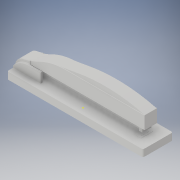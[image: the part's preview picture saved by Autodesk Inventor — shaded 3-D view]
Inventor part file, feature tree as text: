
AUTODESK INVENTOR PART (.ipt)
format: ipt  version: 2017 (Build 210142000, 142)  size: 326,656 bytes
history: native  units: in
note: dims shown in document units (in); Inventor stores cm internally (conversion verified against a paired STEP export)
features: sketch x18, extrude x16, fillet x10, plane x1, other x1
ambient origin geometry x8: Origin, YZ Plane, XZ Plane, XY Plane, X Axis, Y Axis, Z Axis, Center Point
bodies: Solid1 (feature_tree)
feature tree (46):
  extrude  "Extrusion1"  Depth=0.0394in
  fillet  "Fillet1"  Radius=0.0394in
  sketch  "Sketch3"  dims[d2=0.0394in d3=0.0394in d4=0.0394in]
  extrude  "Extrusion2"  Depth=1.5307in
  extrude  "Extrusion3"  Depth=0.3748in TaperAngle=0.0deg
  fillet  "Fillet2"  Radius=0.0787in
  extrude  "Extrusion4"  Depth=1.2687in TaperAngle=0.0deg
  fillet  "Fillet3"  Radius=1.0162in
  extrude  "Extrusion5"  Depth=0.5162in
  extrude  "Extrusion6"  Depth=5.7662in TaperAngle=0.0deg
  fillet  "Fillet4"  Radius=3.0787in
  fillet  "Fillet5"  Radius=3.0787in
  fillet  "Fillet6"  Radius=0.0162in
  fillet  "Fillet7"  Radius=0.0162in
  fillet  "Fillet8"  Radius=0.0162in
  fillet  "Fillet9"  Radius=5.7662in
  extrude  "Extrusion7"  Depth=0.2687in TaperAngle=0.0deg
  extrude  "Extrusion8"  Depth=5.6437in TaperAngle=0.0deg
  extrude  "Extrusion9"  Depth=0.5812in TaperAngle=0.0deg
  sketch  "Sketch12"  dims[d40=0.0591in d41=0.0in d42=16.0787in]
  extrude  "Extrusion10"  Depth=16.0787in
  plane  "Work Plane1"
  extrude  "Extrusion11"  Depth=0.0079in TaperAngle=0.0deg
  extrude  "Extrusion12"  Depth=0.0079in TaperAngle=0.0deg
  fillet  "Fillet10"  [1 undecoded]
  sketch  "Sketch16"
  extrude  "Extrusion13"  [1 undecoded]
  extrude  "Extrusion14"  [1 undecoded]
  extrude  "Extrusion15"  [1 undecoded]
  extrude  "Extrusion16"  [1 undecoded]
  other  "Stapler Bottom "
  sketch  "Sketch4"  dims[d5=0.0394in d6=1.5307in]
  sketch  "Sketch5"  dims[d7=7.2654in d8=0.3748in d9=0.0in d10=0.0787in]
  sketch  "Sketch6"  dims[d11=0.5187in d12=0.0in d13=1.2687in d14=0.0in d15=1.0162in]
  sketch  "Sketch7"  dims[d16=0.5812in d17=0.0in d18=0.5162in]
  sketch  "Sketch8"  dims[d19=6.1437in d20=0.0in d21=0.6437in d22=0.0in d23=3.0787in d24=3.0787in d25=0.0162in d26=0.0162in d27=0.0162in d28=5.7662in]
  sketch  "Sketch9"  dims[d29=6.1437in d30=0.0in d31=0.2687in d32=0.0in]
  sketch  "Sketch10"  dims[d33=0.0812in d34=0.0in d35=5.6437in d36=0.0in]
  sketch  "Sketch11"  dims[d37=-0.4375in d38=0.5812in d39=0.0in]
  sketch  "Sketch13"  dims[d43=0.0118in d44=0.0in d45=0.0079in d46=0.0in]
  sketch  "Sketch14"  dims[d47=0.0079in d48=0.0in d49=0.0079in d50=0.0in]
  sketch  "Sketch15"
  sketch  "Sketch17"
  sketch  "Sketch18"
  sketch  "Sketch19"
  sketch  "Sketch20"
note: 5 required parameter values undecoded (feature->parameter linkage not recoverable at this tier; creation-order binding heuristic only, values carry confidence <= 0.55)
